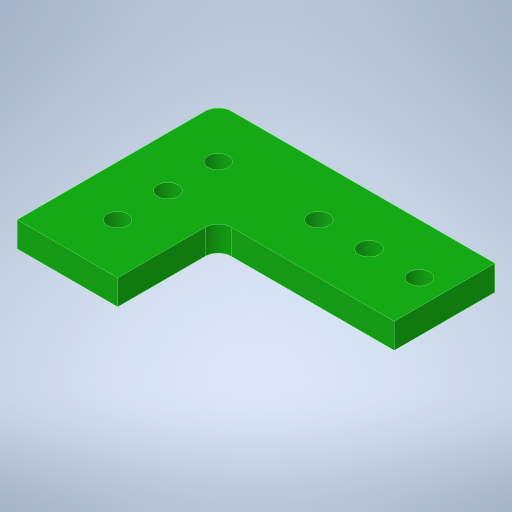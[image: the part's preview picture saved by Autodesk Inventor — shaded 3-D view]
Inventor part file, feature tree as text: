
AUTODESK INVENTOR PART (.ipt)
format: ipt  version: 2023.4 (Build 274418000, 418)  size: 243,712 bytes
history: native  units: in
note: dims shown in document units (in); Inventor stores cm internally (conversion verified against a paired STEP export)
features: sketch x3, extrude x2, hole x1, fillet x1
ambient origin geometry x8: Origin, YZ Plane, XZ Plane, XY Plane, X Axis, Y Axis, Z Axis, Center Point
bodies: Solid1 (feature_tree)
feature tree (7):
  extrude  "Extrusion1"  Depth=2.0in
  extrude  "Extrusion2"  Depth=1.0in
  hole  "Hole2"  [1 undecoded]
  fillet  "Fillet1"  Radius=0.5in
  sketch  "Sketch1"  dims[d0=1.0in d1=2.0in]
  sketch  "Sketch3"  dims[d2=0.25in d3=0.0in d14=1.0in]
  sketch  "Sketch4"  dims[d15=1.75in d16=0.0in d17=0.5in d18=0.5in d19=0.5in d20=1.0in d21=0.5in d22=0.5in d23=0.201in d24=0.75in d25=0.375in d26=0.25in d27=0.5635in d28=1.0in d29=0.8108in d30=0.13in]
note: 1 required parameter value undecoded (feature->parameter linkage not recoverable at this tier; creation-order binding heuristic only, values carry confidence <= 0.55)
